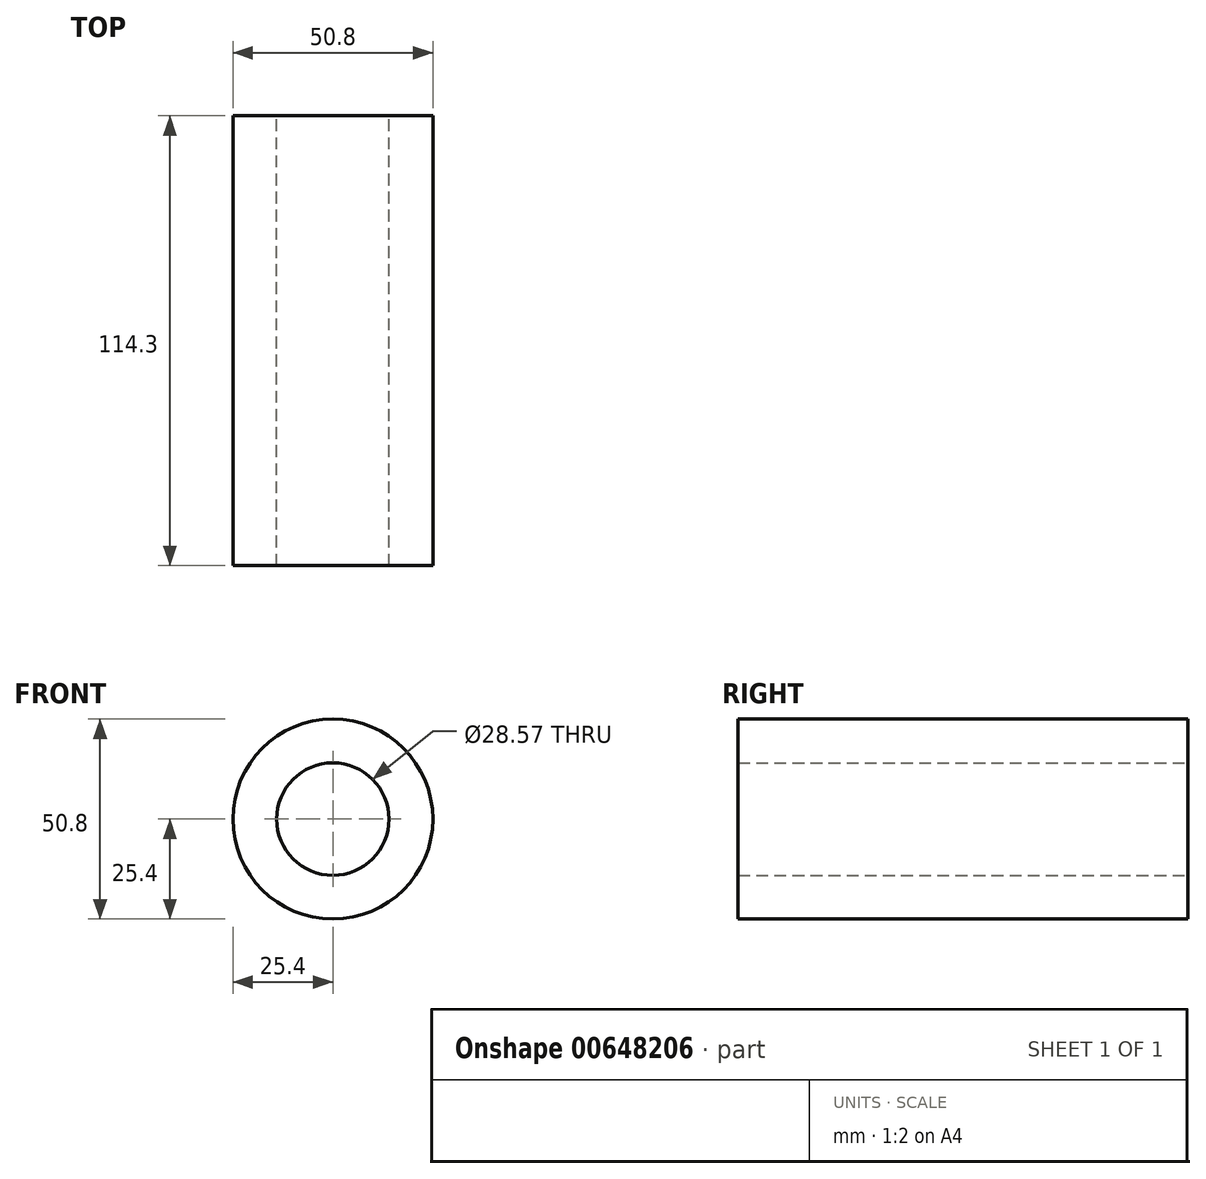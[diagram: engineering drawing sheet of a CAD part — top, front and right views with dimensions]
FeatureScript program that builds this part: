
annotation { "Feature Type Name" : "Feature", "Feature Type Description" : "" }
export const myFeature = defineFeature(function(context is Context, id is Id, definition is map)
    precondition{}
    {
        {
            var Q0;
            Q0=qCreatedBy(makeId("Front.planeOp"),FACE);
            var sketch = newSketch(context, id + "F0", { "sketchPlane" : qUnion([Q0])});
            skCircle(sketch, "E0", {"center": v(0, 0) * mm, "radius": 25.4 * mm});
            skCircle(sketch, "E1", {"center": v(0, 0) * mm, "radius": 14.29 * mm});
            skSolve(sketch);
        }
        {
            var Q0;
            Q0=qSketchRegion(id+"F0",true);
            extrude(context, id + "F1", {"entities" : qUnion([Q0]), "depth" : 114.3 * mm, "offsetDistance" : 25.4 * mm});
        }
    });
